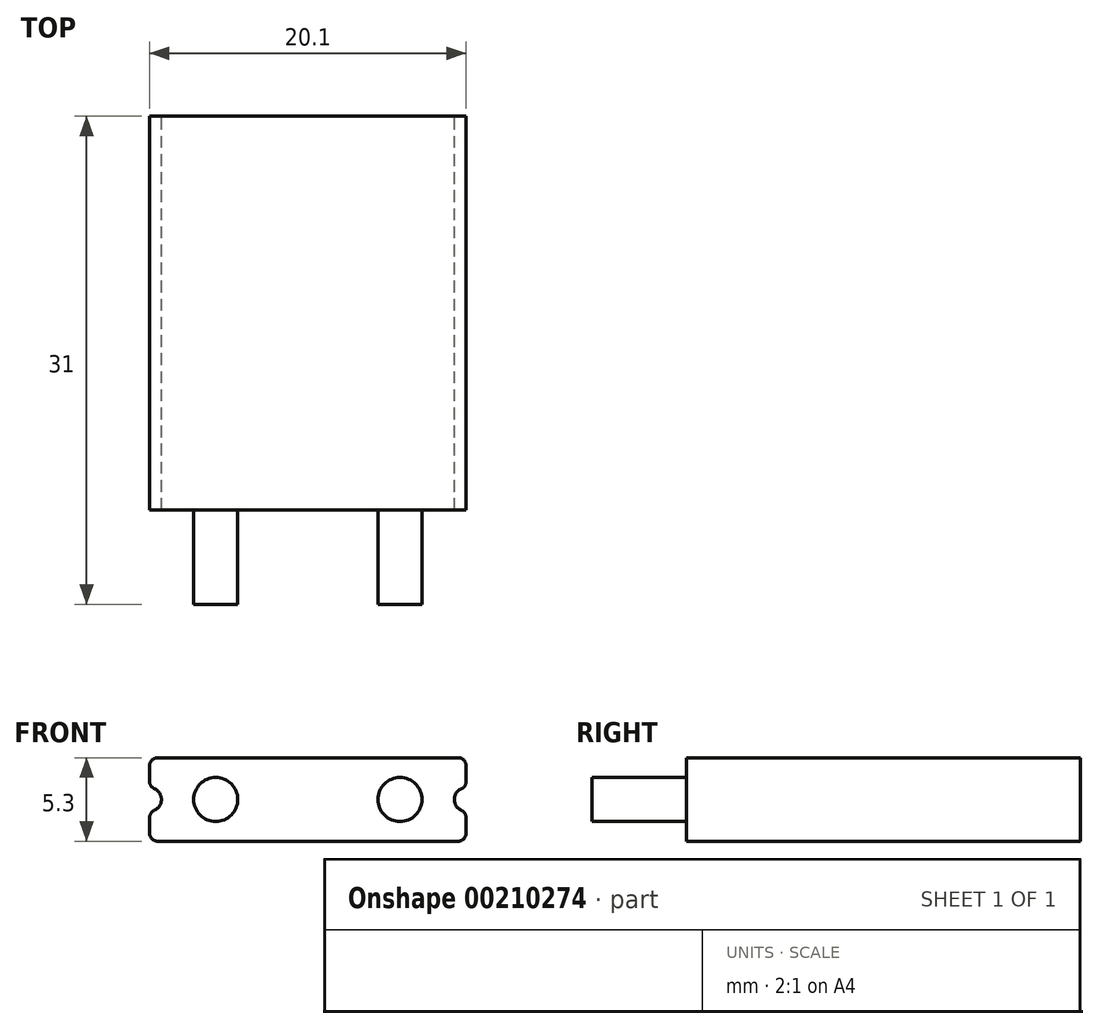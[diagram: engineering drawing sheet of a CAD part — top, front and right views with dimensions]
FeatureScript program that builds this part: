
annotation { "Feature Type Name" : "Feature", "Feature Type Description" : "" }
export const myFeature = defineFeature(function(context is Context, id is Id, definition is map)
    precondition{}
    {
        {
            var Q0;
            Q0=qCreatedBy(makeId("Front.planeOp"),FACE);
            var sketch = newSketch(context, id + "F0", { "sketchPlane" : qUnion([Q0])});
            skLineSegment(sketch, "E0.bottom", {"start": v(0, 0) * mm, "end": v(20.1, 0) * mm});
            skLineSegment(sketch, "E0.top", {"start": v(0, 5.3) * mm, "end": v(20.1, 5.3) * mm});
            skLineSegment(sketch, "E0.left", {"start": v(0, 0) * mm, "end": v(0, 1.9) * mm});
            skLineSegment(sketch, "E0.right", {"start": v(20.1, 0) * mm, "end": v(20.1, 1.9) * mm});
            skArc(sketch, "E1", {"start": v(0, 1.9) * mm, "mid": v(0.75, 2.65) * mm, "end": v(0, 3.4) * mm});
            skArc(sketch, "E2", {"start": v(20.1, 3.4) * mm, "mid": v(19.35, 2.65) * mm, "end": v(20.1, 1.9) * mm});
            skLineSegment(sketch, "E3.trimOffspring", {"start": v(0, 3.4) * mm, "end": v(0, 5.3) * mm});
            skLineSegment(sketch, "E4.trimOffspring", {"start": v(20.1, 3.4) * mm, "end": v(20.1, 5.3) * mm});
            skSolve(sketch);
        }
        {
            var Q0;
            Q0=qSketchRegion(id+"F0",true);
            extrude(context, id + "F1", {"entities" : qUnion([Q0]), "depth" : 25 * mm});
        }
        {
            var Q0;
            Q0=makeQuery(id+"F1.opExtrude","CAP_FACE",FACE,{"disambiguationData":[OSD([sQuery(id+"F0.wireOp",EDGE,"E0.bottom"),sQuery(id+"F0.wireOp",EDGE,"E0.top"),sQuery(id+"F0.wireOp",EDGE,"E0.left"),sQuery(id+"F0.wireOp",EDGE,"E0.right"),sQuery(id+"F0.wireOp",EDGE,"E1"),sQuery(id+"F0.wireOp",EDGE,"E2"),sQuery(id+"F0.wireOp",EDGE,"E3.trimOffspring"),sQuery(id+"F0.wireOp",EDGE,"E4.trimOffspring")])],"isStart":false});
            var sketch = newSketch(context, id + "F2", { "sketchPlane" : qUnion([Q0])});
            skCircle(sketch, "E5", {"center": v(4.2, 2.65) * mm, "radius": 1.4 * mm});
            skCircle(sketch, "E6", {"center": v(15.9, 2.65) * mm, "radius": 1.4 * mm});
            skLineSegment(sketch, "E7", {"start": v(20.1, 2.65) * mm, "end": v(0, 2.65) * mm, "construction": true});
            skSolve(sketch);
        }
        {
            var Q0;
            Q0=qSketchRegion(id+"F2",true);
            extrude(context, id + "F3", {"entities" : qUnion([Q0]), "operationType" : NewBodyOperationType.ADD, "depth" : 6 * mm});
        }
        {
            var Q0;
            Q0=makeQuery(id+"F1.opExtrude","SWEPT_EDGE",EDGE,{"disambiguationData":[OSD([sQuery(id+"F0.wireOp",EDGE,"E0.top"),sQuery(id+"F0.wireOp",EDGE,"E4.trimOffspring")])]});
            var Q1;
            Q1=makeQuery(id+"F1.opExtrude","SWEPT_EDGE",EDGE,{"disambiguationData":[OSD([sQuery(id+"F0.wireOp",EDGE,"E2"),sQuery(id+"F0.wireOp",EDGE,"E4.trimOffspring")])]});
            var Q2;
            Q2=makeQuery(id+"F1.opExtrude","SWEPT_EDGE",EDGE,{"disambiguationData":[OSD([sQuery(id+"F0.wireOp",EDGE,"E0.right"),sQuery(id+"F0.wireOp",EDGE,"E2")])]});
            var Q3;
            Q3=makeQuery(id+"F1.opExtrude","SWEPT_EDGE",EDGE,{"disambiguationData":[OSD([sQuery(id+"F0.wireOp",EDGE,"E0.bottom"),sQuery(id+"F0.wireOp",EDGE,"E0.right")])]});
            var Q4;
            Q4=makeQuery(id+"F1.opExtrude","SWEPT_EDGE",EDGE,{"disambiguationData":[OSD([sQuery(id+"F0.wireOp",EDGE,"E0.top"),sQuery(id+"F0.wireOp",EDGE,"E3.trimOffspring")])]});
            var Q5;
            Q5=makeQuery(id+"F1.opExtrude","SWEPT_EDGE",EDGE,{"disambiguationData":[OSD([sQuery(id+"F0.wireOp",EDGE,"E0.bottom"),sQuery(id+"F0.wireOp",EDGE,"E0.left")])]});
            var Q6;
            Q6=makeQuery(id+"F1.opExtrude","SWEPT_EDGE",EDGE,{"disambiguationData":[OSD([sQuery(id+"F0.wireOp",EDGE,"E0.left"),sQuery(id+"F0.wireOp",EDGE,"E1")])]});
            var Q7;
            Q7=makeQuery(id+"F1.opExtrude","SWEPT_EDGE",EDGE,{"disambiguationData":[OSD([sQuery(id+"F0.wireOp",EDGE,"E1"),sQuery(id+"F0.wireOp",EDGE,"E3.trimOffspring")])]});
            fillet(context, id + "F4", {"entities" : qUnion([Q0, Q1, Q2, Q3, Q4, Q5, Q6, Q7]), "radius" : .5 * mm, "tangentPropagation" : true, "allowEdgeOverflow" : false});
        }
    });
